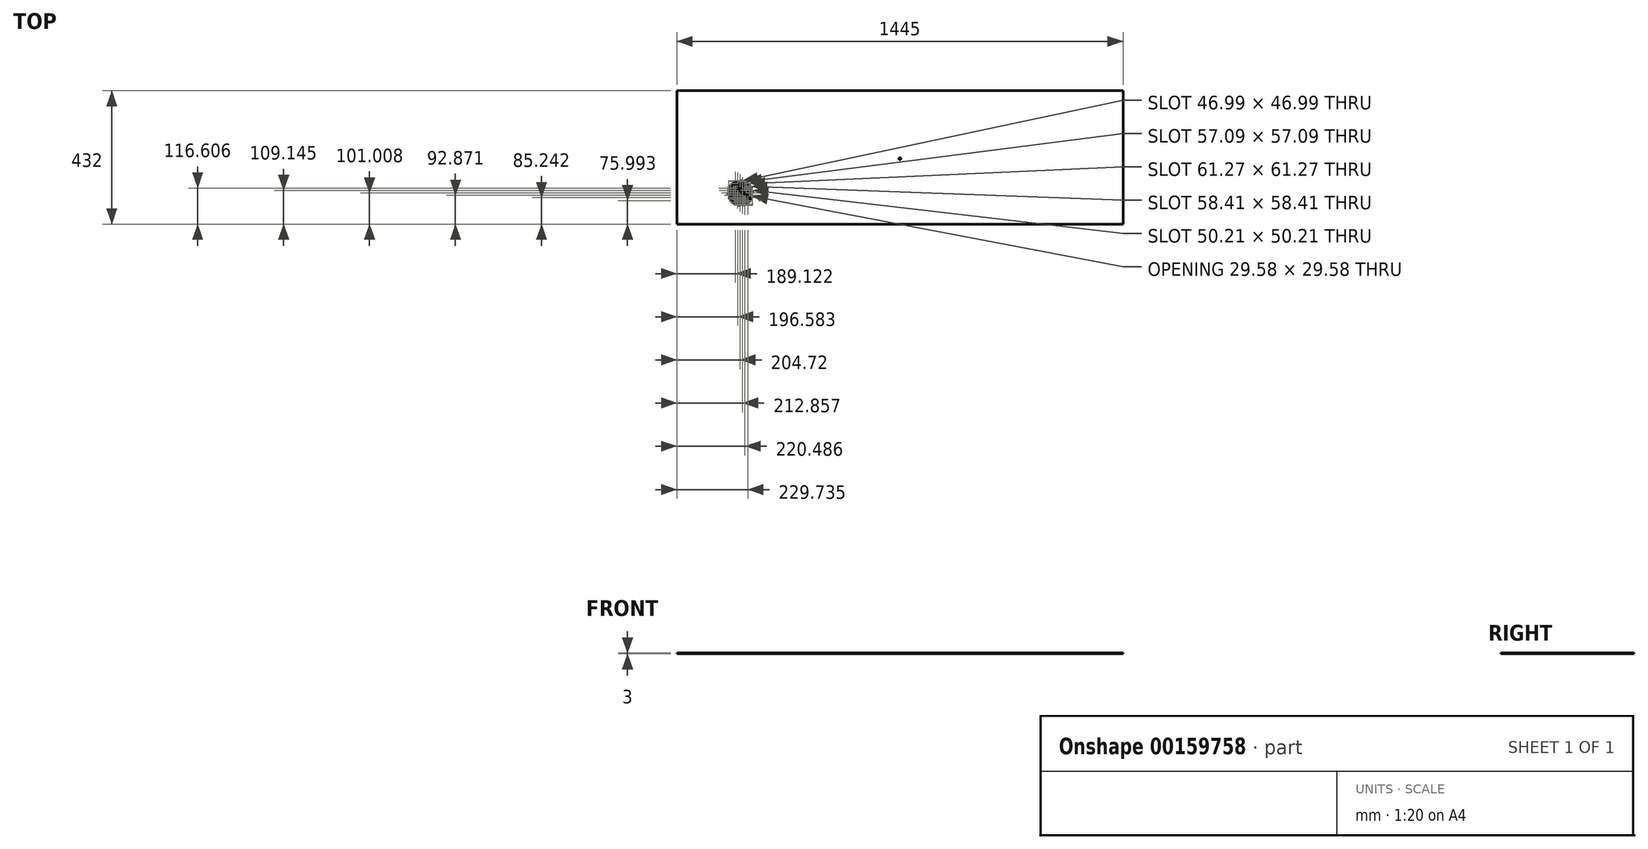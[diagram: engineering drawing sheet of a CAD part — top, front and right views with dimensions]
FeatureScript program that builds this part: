
annotation { "Feature Type Name" : "Feature", "Feature Type Description" : "" }
export const myFeature = defineFeature(function(context is Context, id is Id, definition is map)
    precondition{}
    {
        {
            var Q0;
            Q0=qCreatedBy(makeId("Top.planeOp"),FACE);
            var sketch = newSketch(context, id + "F0", { "sketchPlane" : qUnion([Q0])});
            skLineSegment(sketch, "E0", {"start": v(-624.43, -42.04) * mm, "end": v(-624.43, 389.96) * mm});
            skLineSegment(sketch, "E1", {"start": v(-624.43, 389.96) * mm, "end": v(-157.43, 389.96) * mm});
            skLineSegment(sketch, "E2", {"start": v(-157.43, 389.96) * mm, "end": v(353.57, 389.96) * mm});
            skLineSegment(sketch, "E3", {"start": v(353.57, 389.96) * mm, "end": v(820.57, 389.96) * mm});
            skLineSegment(sketch, "E4", {"start": v(820.57, 389.96) * mm, "end": v(820.57, -42.04) * mm});
            skLineSegment(sketch, "E5", {"start": v(820.57, -42.04) * mm, "end": v(-624.43, -42.04) * mm});
            skCircle(sketch, "E6", {"center": v(98.07, 169.96) * mm, "radius": 3 * mm});
            skLineSegment(sketch, "E7", {"start": v(-157.43, 389.96) * mm, "end": v(-157.43, 388.96) * mm});
            skLineSegment(sketch, "E8", {"start": v(353.57, 389.96) * mm, "end": v(353.57, 388.96) * mm});
            skLineSegment(sketch, "E9", {"start": v(353.57, -42.04) * mm, "end": v(353.57, -41.04) * mm});
            skLineSegment(sketch, "E10", {"start": v(-157.43, -42.04) * mm, "end": v(-157.43, -41.04) * mm});
            skArc(sketch, "E11", {"start": v(-458.8, 58.95) * mm, "mid": v(-458.69, 55) * mm, "end": v(-458.19, 51.07) * mm});
            skLineSegment(sketch, "E12", {"start": v(-457.3, 68.93) * mm, "end": v(-429.67, 96.56) * mm});
            skLineSegment(sketch, "E13.0", {"start": v(-458.8, 58.95) * mm, "end": v(-419.7, 98.05) * mm});
            skLineSegment(sketch, "E14.0", {"start": v(-458.19, 51.07) * mm, "end": v(-411.81, 97.45) * mm});
            skLineSegment(sketch, "E15.0", {"start": v(-456.4, 44.38) * mm, "end": v(-405.12, 95.65) * mm});
            skLineSegment(sketch, "E16.0", {"start": v(-453.73, 38.56) * mm, "end": v(-399.3, 92.99) * mm});
            skLineSegment(sketch, "E17.0", {"start": v(-450.34, 33.46) * mm, "end": v(-394.2, 89.6) * mm});
            skLineSegment(sketch, "E18.0", {"start": v(-445.57, 28.33) * mm, "end": v(-389.08, 84.83) * mm});
            skLineSegment(sketch, "E19.0", {"start": v(-440.78, 24.64) * mm, "end": v(-385.38, 80.04) * mm});
            skLineSegment(sketch, "E20.0", {"start": v(-435.3, 21.62) * mm, "end": v(-382.37, 74.57) * mm});
            skLineSegment(sketch, "E21.0", {"start": v(-429.05, 19.4) * mm, "end": v(-380.14, 68.3) * mm});
            skLineSegment(sketch, "E22.0", {"start": v(-420.45, 18.1) * mm, "end": v(-378.84, 59.7) * mm});
            skLineSegment(sketch, "E23.0", {"start": v(-409.49, 19.16) * mm, "end": v(-379.9, 48.74) * mm});
            skArc(sketch, "E24.trimOffspring", {"start": v(-429.67, 96.56) * mm, "mid": v(-447.09, 86.35) * mm, "end": v(-457.3, 68.93) * mm});
            skArc(sketch, "E25.trimOffspring", {"start": v(-411.81, 97.45) * mm, "mid": v(-415.74, 97.94) * mm, "end": v(-419.7, 98.05) * mm});
            skArc(sketch, "E26.trimOffspring", {"start": v(-456.4, 44.38) * mm, "mid": v(-455.18, 41.42) * mm, "end": v(-453.73, 38.56) * mm});
            skArc(sketch, "E27.trimOffspring", {"start": v(-450.34, 33.46) * mm, "mid": v(-448.07, 30.8) * mm, "end": v(-445.57, 28.33) * mm});
            skArc(sketch, "E28.trimOffspring", {"start": v(-399.3, 92.99) * mm, "mid": v(-402.16, 94.43) * mm, "end": v(-405.12, 95.65) * mm});
            skArc(sketch, "E29.trimOffspring", {"start": v(-389.08, 84.83) * mm, "mid": v(-391.53, 87.33) * mm, "end": v(-394.2, 89.6) * mm});
            skArc(sketch, "E30.trimOffspring", {"start": v(-440.78, 24.64) * mm, "mid": v(-438.1, 23.02) * mm, "end": v(-435.3, 21.62) * mm});
            skArc(sketch, "E31.trimOffspring", {"start": v(-429.05, 19.4) * mm, "mid": v(-424.79, 18.51) * mm, "end": v(-420.45, 18.1) * mm});
            skArc(sketch, "E32.trimOffspring", {"start": v(-382.37, 74.57) * mm, "mid": v(-383.77, 77.36) * mm, "end": v(-385.38, 80.04) * mm});
            skArc(sketch, "E33.trimOffspring", {"start": v(-378.84, 59.7) * mm, "mid": v(-379.25, 64.04) * mm, "end": v(-380.14, 68.3) * mm});
            skArc(sketch, "E34.trimOffspring", {"start": v(-409.49, 19.16) * mm, "mid": v(-390.52, 29.78) * mm, "end": v(-379.9, 48.74) * mm});
            skSolve(sketch);
        }
        {
            var Q0;
            {var subQ4=sQuery(id+"F0.wireOp",EDGE,"E0");Q0=makeQuery(id+"F0.imprint","IMPRINT",FACE,{"disambiguationData":[TD([[makeQuery(id+"F0.imprint","IMPRINT",EDGE,{"derivedFrom":subQ4}),-1.0]])]});}
            extrude(context, id + "F1", {"entities" : qUnion([Q0]), "depth" : 3 * mm});
        }
    });
